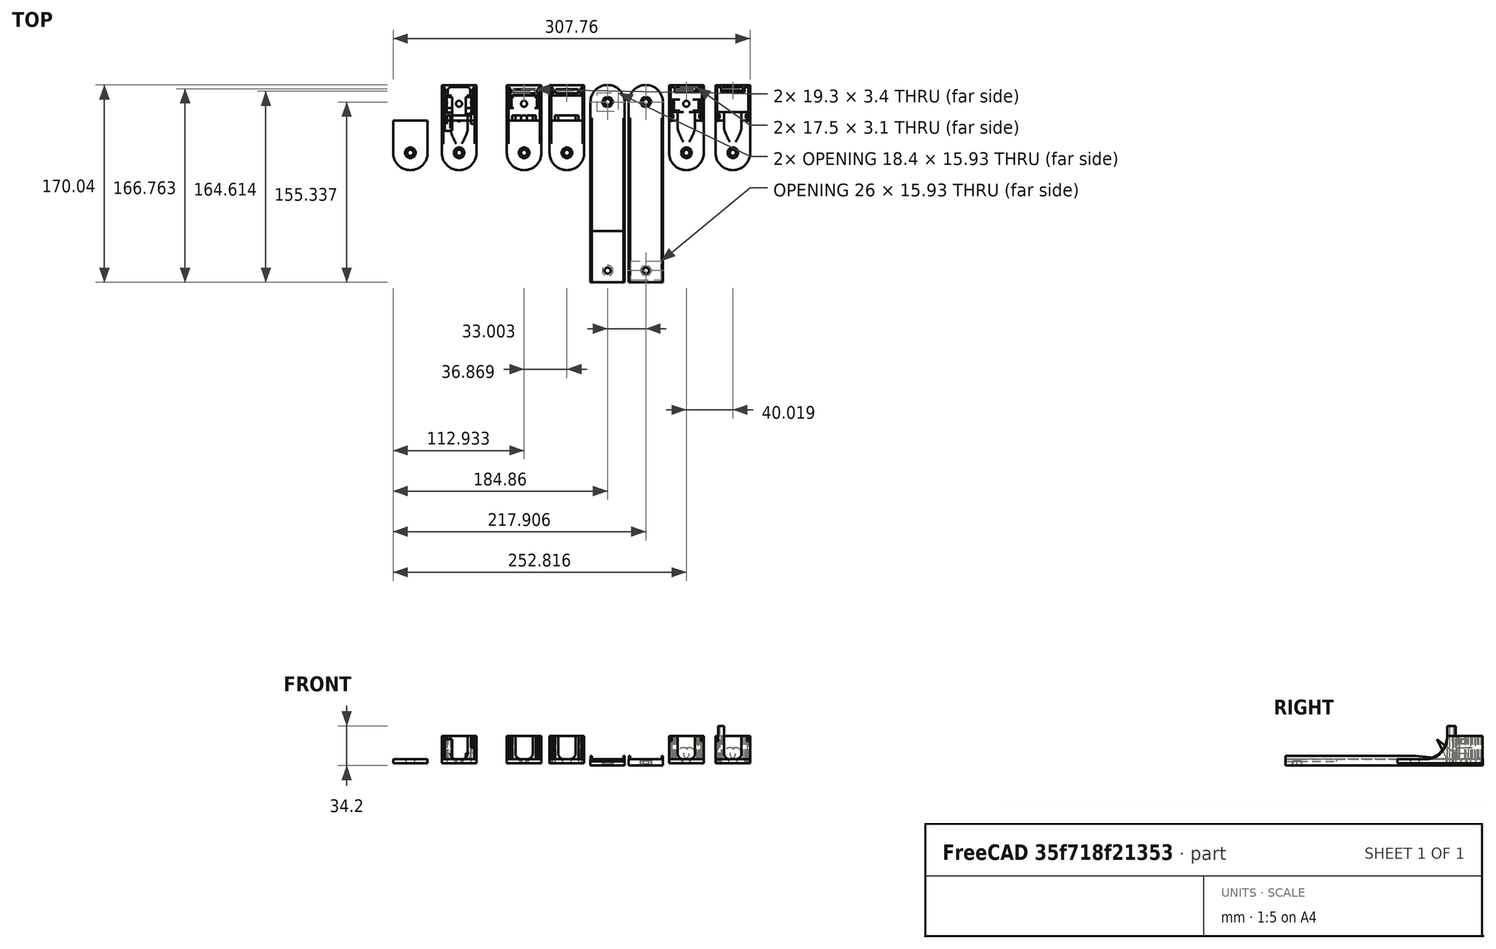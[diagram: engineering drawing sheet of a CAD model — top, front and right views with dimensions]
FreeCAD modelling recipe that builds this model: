
FCSTD DOCUMENT  (FreeCAD 0.18.4R)
Label: tmp
License: All rights reserved
LicenseURL: http://en.wikipedia.org/wiki/All_rights_reserved
objects: Part::Extrusion×56, Part::Part2DObjectPython×44, Part::Cut×42, Part::Feature×31, Part::FeaturePython×31, Part::MultiFuse×22, App::DocumentObjectGroup×10, Part::Cone×1
note: 227 computed .brp shape members not serialized (recipe doc carries the construction recipe); baked Part::Feature solids carry a one-line shape summary decoded from their .brp

FEATURE [Part::MultiFuse] Fusion
FEATURE [Part::Part2DObjectPython] Rectangle008  # Draft 2D object (typed FeaturePython)
  ChamferSize = 0
  Columns = 1
  FilletRadius = 0
  Height = 8.73003
  Length = 8.98196
  MakeFace = true
  Placement = pos=(-698.896,-12.7746,7.63603) rot=(0.57735,0.57735,0.57735;2.0944rad)
  Rows = 1
FEATURE [Part::Part2DObjectPython] Circle  # Draft 2D object (typed FeaturePython)
  FirstAngle = 0
  LastAngle = 0
  MakeFace = true
  Placement = pos=(-707.421,-8.97512,-3.63395) rot=(0,0,1;0rad)
  Radius = 2.6
  Support = -> [Fusion]
FEATURE [Part::Extrusion] Extrusion
  Base = -> Circle
  Dir = (0,0,-104.516)
  DirMode = 0
  FaceMakerClass = Part::FaceMakerBullseye
  LengthFwd = 0
  LengthRev = 0
  Solid = true
  Symmetric = false
FEATURE [Part::Feature] Face001
  Placement = pos=(-176.911,1.4e-14,3.6e-14) rot=(0,0,1;0rad)
  shape: bbox 5 x 7.4 x 3e-07 mm, 1 faces, 0 solids (baked)
FEATURE [Part::Cut] Cut004006005004002008019023005014
FEATURE [Part::Feature] Face003
  Placement = pos=(86.8688,-7e-15,-1.8e-14) rot=(0,0,1;0rad)
  shape: bbox 3.179 x 4.601 x 4.951e-06 mm, 1 faces, 0 solids (baked)
FEATURE [Part::Feature] Face
  shape: bbox 29.86 x 30.4 x 3e-07 mm, 1 faces, 0 solids (baked)
FEATURE [Part::Extrusion] Extrusion003
  Base = -> Face
  Dir = (1.2e-15,1.59e-14,-8.7)
  DirMode = 0
  FaceMakerClass = Part::FaceMakerBullseye
  LengthFwd = 0
  LengthRev = 0
  Solid = true
  Symmetric = false
FEATURE [Part::Feature] Face004
  Placement = pos=(86.8688,-7e-15,-1.8e-14) rot=(0,0,1;0rad)
  shape: bbox 3.308 x 4.601 x 4.951e-06 mm, 1 faces, 0 solids (baked)
FEATURE [Part::Part2DObjectPython] Rectangle  # Draft 2D object (typed FeaturePython)
  ChamferSize = 0
  Columns = 1
  FilletRadius = 0
  Height = 3.10055
  Length = 17.5
  MakeFace = true
  Placement = pos=(-716.1,2.42323,16.3661) rot=(0,0,1;0rad)
  Rows = 1
FEATURE [Part::Extrusion] Extrusion001
  Base = -> Rectangle
  Dir = (2.96e-14,4.57e-14,-64.3884)
  DirMode = 0
  FaceMakerClass = Part::FaceMakerBullseye
  LengthFwd = 0
  LengthRev = 0
  Solid = true
  Symmetric = false
FEATURE [Part::Feature] Face006
  Placement = pos=(-756.265,0.89093,29.4029) rot=(1,0,0;1.5708rad)
  shape: bbox 4.243e-07 x 5.5 x 4 mm, 1 faces, 0 solids (baked)
FEATURE [Part::Extrusion] Extrusion019
  Base = -> Face006
  Dir = (-0.5,3.05e-14,0)
  DirMode = 0
  FaceMakerClass = Part::FaceMakerBullseye
  LengthFwd = 0
  LengthRev = 0
  Solid = true
  Symmetric = false
FEATURE [Part::Cut] Cut
  Base = -> Fusion
  Tool = -> Extrusion
FEATURE [Part::Cut] Cut001
  Base = -> Cut
  Placement = pos=(135.846,-2.34e-13,1.41e-13) rot=(0,0,1;0rad)
  Tool = -> Extrusion001
FEATURE [Part::Extrusion] Extrusion006
  Base = -> Face003
  Dir = (1.13e-14,3.35e-14,-10.0532)
  DirMode = 0
  FaceMakerClass = Part::FaceMakerBullseye
  LengthFwd = 0
  LengthRev = 0
  Solid = true
  Symmetric = false
FEATURE [Part::Extrusion] Extrusion007
  Base = -> Face004
  Dir = (1.43e-14,4.44e-14,-13.335)
  DirMode = 0
  FaceMakerClass = Part::FaceMakerBullseye
  LengthFwd = 0
  LengthRev = 0
  Solid = true
  Symmetric = false
FEATURE [Part::Feature] Face005
  Placement = pos=(-756.265,0.89093,29.4029) rot=(1,0,0;1.5708rad)
  shape: bbox 4.243e-07 x 5 x 4 mm, 1 faces, 0 solids (baked)
FEATURE [Part::Extrusion] Extrusion018
  Base = -> Face005
  Dir = (0.5,-3.05e-14,0)
  DirMode = 0
  FaceMakerClass = Part::FaceMakerBullseye
  LengthFwd = 0
  LengthRev = 0
  Solid = true
  Symmetric = false
FEATURE [Part::Cut] Cut004006005004002008019023005004
  Placement = pos=(-176.911,1.4e-14,3.6e-14) rot=(0,0,1;0rad)
FEATURE [Part::MultiFuse] Fusion002005
  Placement = pos=(86.8688,-7.1e-15,-1.78e-14) rot=(0,0,1;0rad)
FEATURE [Part::Feature] Face002
  Placement = pos=(-176.911,1.4e-14,3.6e-14) rot=(0,0,1;0rad)
  shape: bbox 5 x 7.4 x 3e-07 mm, 1 faces, 0 solids (baked)
FEATURE [Part::Extrusion] Extrusion005
  Base = -> Face002
  Dir = (2.184e-13,5.98e-14,-8.7)
  DirMode = 0
  FaceMakerClass = Part::FaceMakerBullseye
  LengthFwd = 0
  LengthRev = 0
  Solid = true
  Symmetric = false
FEATURE [Part::Extrusion] Extrusion004
  Base = -> Face001
  Dir = (-2.51e-14,6.47e-14,-8.7)
  DirMode = 0
  FaceMakerClass = Part::FaceMakerBullseye
  LengthFwd = 0
  LengthRev = 0
  Solid = true
  Symmetric = false
FEATURE [Part::Part2DObjectPython] Rectangle007  # Draft 2D object (typed FeaturePython)
  ChamferSize = 0
  Columns = 1
  FilletRadius = 0
  Height = 2
  Length = 2
  MakeFace = true
  Placement = pos=(-698.896,-12.7746,-3.63395) rot=(1,0,0;1.5708rad)
  Rows = 1
FEATURE [Part::Extrusion] Extrusion015
  Base = -> Rectangle007
  Dir = (6.992e-13,9.7,-2.2e-15)
  DirMode = 0
  FaceMakerClass = Part::FaceMakerBullseye
  LengthFwd = 0
  LengthRev = 0
  Solid = true
  Symmetric = false
FEATURE [Part::Part2DObjectPython] Rectangle009  # Draft 2D object (typed FeaturePython)
  ChamferSize = 0
  Columns = 1
  FilletRadius = 0
  Height = 8.52247
  Length = 8.85872
  MakeFace = true
  Placement = pos=(-723.896,-3.91585,7.84359) rot=(0.57735,-0.57735,-0.57735;2.0944rad)
  Rows = 1
FEATURE [Part::Part2DObjectPython] Rectangle001  # Draft 2D object (typed FeaturePython)
  ChamferSize = 0
  Columns = 1
  FilletRadius = 0
  Height = 3.10055
  Length = 17.5
  MakeFace = true
  Placement = pos=(-676.081,2.42323,25.0661) rot=(0,0,1;0rad)
  Rows = 1
  Support = -> [Cut001]
FEATURE [Part::Extrusion] Extrusion002
  Base = -> Rectangle001
  Dir = (2.04e-14,3.15e-14,-44.3555)
  DirMode = 0
  FaceMakerClass = Part::FaceMakerBullseye
  LengthFwd = 0
  LengthRev = 0
  Solid = true
  Symmetric = false
FEATURE [Part::Cut] Cut004006005004002008019023005005
  Base = -> Cut004006005004002008019023005004
  Tool = -> Extrusion002
FEATURE [Part::Cut] Cut004006005004002008019023005006
  Base = -> Cut004006005004002008019023005005
  Tool = -> Extrusion003
FEATURE [Part::Cut] Cut004006005004002008019023005007
  Base = -> Cut004006005004002008019023005006
  Placement = pos=(135.846,-2.34e-13,1.41e-13) rot=(0,0,1;0rad)
  Tool = -> Extrusion005
FEATURE [Part::Cut] Cut004006005004002008019023005008
  Base = -> Cut004006005004002008019023005007
  Tool = -> Extrusion004
FEATURE [Part::MultiFuse] Fusion005002002014004003003002009002010004002003006003008008004007002004006006004008003005011006
  Placement = pos=(-82.9949,0,-5e-15) rot=(0,0,1;0rad)
  Shapes = -> [Cut004006005004002008019023005007]
FEATURE [Part::Part2DObjectPython] Rectangle002  # Draft 2D object (typed FeaturePython)
  ChamferSize = 0
  Columns = 1
  FilletRadius = 0
  Height = 20
  Length = 5.5
  MakeFace = true
  Placement = pos=(-705.896,-12.7746,-3.63395) rot=(1,0,0;1.5708rad)
  Rows = 1
  Support = -> [Cut004006005004002008019023005014]
FEATURE [Part::Extrusion] Extrusion008
  Base = -> Rectangle002
  Dir = (6.992e-13,9.7,-2.2e-15)
  DirMode = 0
  FaceMakerClass = Part::FaceMakerBullseye
  LengthFwd = 0
  LengthRev = 0
  Solid = true
  Symmetric = false
FEATURE [Part::Cut] Cut004006005004002008019023005017
  Base = -> Cut004006005004002008019023005014
  Tool = -> Extrusion008
FEATURE [Part::Part2DObjectPython] Rectangle003  # Draft 2D object (typed FeaturePython)
  ChamferSize = 0
  Columns = 1
  FilletRadius = 0
  Height = 20
  Length = 5.5
  MakeFace = true
  Placement = pos=(-716.896,-12.7746,16.3661) rot=(0,0.707107,-0.707107;3.14159rad)
  Rows = 1
  Support = -> [Cut004006005004002008019023005017]
FEATURE [Part::Extrusion] Extrusion009
  Base = -> Rectangle003
  Dir = (6.24e-13,9.7,-4.3e-15)
  DirMode = 0
  FaceMakerClass = Part::FaceMakerBullseye
  LengthFwd = 0
  LengthRev = 0
  Solid = true
  Symmetric = false
FEATURE [Part::Cut] Cut004006005004002008019023005018
  Base = -> Cut004006005004002008019023005017
  Tool = -> Extrusion009
FEATURE [Part::Part2DObjectPython] Rectangle005  # Draft 2D object (typed FeaturePython)
  ChamferSize = 0
  Columns = 1
  FilletRadius = 0
  Height = 2
  Length = 2
  MakeFace = true
  Placement = pos=(-720.396,-12.7746,-1.63395) rot=(0,0.707107,-0.707107;3.14159rad)
  Rows = 1
  Support = -> [Cut004006005004002008019023005018]
FEATURE [Part::Part2DObjectPython] Circle001  # Draft 2D object (typed FeaturePython)
  FirstAngle = 0
  LastAngle = 0
  MakeFace = true
  Placement = pos=(-725.896,-12.7746,-1.63395) rot=(0,0.707107,-0.707107;3.14159rad)
  Radius = 2
  Support = -> [Cut004006005004002008019023005018]
FEATURE [Part::Extrusion] Extrusion012
  Base = -> Rectangle005
  Dir = (6.24e-13,9.7,-4.3e-15)
  DirMode = 0
  FaceMakerClass = Part::FaceMakerBullseye
  LengthFwd = 0
  LengthRev = 0
  Solid = true
  Symmetric = false
FEATURE [Part::Part2DObjectPython] Circle002  # Draft 2D object (typed FeaturePython)
  FirstAngle = 0
  LastAngle = 0
  MakeFace = true
  Placement = pos=(-720.396,-12.7746,-1.63395) rot=(0,0.707107,-0.707107;3.14159rad)
  Radius = 2
  Support = -> [Extrusion012]
FEATURE [Part::Extrusion] Extrusion013
  Base = -> Circle002
  Dir = (6.367e-13,9.7,-2.2e-15)
  DirMode = 0
  FaceMakerClass = Part::FaceMakerBullseye
  LengthFwd = 0
  LengthRev = 0
  Solid = true
  Symmetric = false
FEATURE [Part::Part2DObjectPython] Rectangle004  # Draft 2D object (typed FeaturePython)
  ChamferSize = 0
  Columns = 1
  FilletRadius = 0
  Height = 2
  Length = 2
  MakeFace = true
  Placement = pos=(-723.896,-12.7746,-1.63395) rot=(0,0.707107,-0.707107;3.14159rad)
  Rows = 1
  Support = -> [Cut004006005004002008019023005018]
FEATURE [Part::Extrusion] Extrusion010
  Base = -> Rectangle004
  Dir = (6.24e-13,9.7,-4.3e-15)
  DirMode = 0
  FaceMakerClass = Part::FaceMakerBullseye
  LengthFwd = 0
  LengthRev = 0
  Solid = true
  Symmetric = false
FEATURE [Part::Extrusion] Extrusion011
  Base = -> Circle001
  Dir = (6.367e-13,9.7,-2.2e-15)
  DirMode = 0
  FaceMakerClass = Part::FaceMakerBullseye
  LengthFwd = 0
  LengthRev = 0
  Solid = true
  Symmetric = false
FEATURE [Part::Cut] Cut004006005004002008019023005019
  Base = -> Extrusion010
  Tool = -> Extrusion011
FEATURE [Part::MultiFuse] Fusion005002002014004003003002009002010004002003006003008008004007002004003
  Placement = pos=(-677.592,-2.54468,-4) rot=(0,0,1;0rad)
FEATURE [Part::Cut] Cut004006005004002008019023005020
  Base = -> Extrusion012
  Tool = -> Extrusion013
FEATURE [Part::MultiFuse] Fusion005002002014004003003002009002010004002003006003008008004007002004006006004008003005011007
  Shapes = -> [Cut004006005004002008019023005019,Cut004006005004002008019023005020,Cut004006005004002008019023005018]
FEATURE [Part::Part2DObjectPython] Rectangle006  # Draft 2D object (typed FeaturePython)
  ChamferSize = 0
  Columns = 1
  FilletRadius = 0
  Height = 2
  Length = 2
  MakeFace = true
  Placement = pos=(-702.396,-12.7746,-3.63395) rot=(1,0,0;1.5708rad)
  Rows = 1
  Support = -> [Fusion005002002014004003003002009002010004002003006003008008004007002004006006004008003005011007]
FEATURE [Part::Extrusion] Extrusion014
  Base = -> Rectangle006
  Dir = (6.992e-13,9.7,-2.2e-15)
  DirMode = 0
  FaceMakerClass = Part::FaceMakerBullseye
  LengthFwd = 0
  LengthRev = 0
  Solid = true
  Symmetric = false
FEATURE [Part::Part2DObjectPython] Circle003  # Draft 2D object (typed FeaturePython)
  FirstAngle = 0
  LastAngle = 0
  MakeFace = true
  Placement = pos=(-702.396,-12.7746,-1.63395) rot=(1,0,0;1.5708rad)
  Radius = 2
  Support = -> [Rectangle006]
FEATURE [Part::Extrusion] Extrusion017
  Base = -> Circle003
  Dir = (6.992e-13,9.7,-2.2e-15)
  DirMode = 0
  FaceMakerClass = Part::FaceMakerBullseye
  LengthFwd = 0
  LengthRev = 0
  Solid = true
  Symmetric = false
FEATURE [Part::Cut] Cut004006005004002008019023005021
  Base = -> Extrusion014
  Tool = -> Extrusion017
FEATURE [Part::Part2DObjectPython] Circle004  # Draft 2D object (typed FeaturePython)
  FirstAngle = 0
  LastAngle = 0
  MakeFace = true
  Placement = pos=(-696.896,-12.7746,-1.63395) rot=(1,0,0;1.5708rad)
  Radius = 2
  Support = -> [Fusion005002002014004003003002009002010004002003006003008008004007002004006006004008003005011007]
FEATURE [Part::Extrusion] Extrusion016
  Base = -> Circle004
  Dir = (6.992e-13,9.7,-2.2e-15)
  DirMode = 0
  FaceMakerClass = Part::FaceMakerBullseye
  LengthFwd = 0
  LengthRev = 0
  Solid = true
  Symmetric = false
FEATURE [Part::Cut] Cut004006005004002008019023005022
  Base = -> Extrusion015
  Tool = -> Extrusion016
FEATURE [Part::MultiFuse] Fusion005002002014004003003002009002010004002003006003008008004007002004006006004008003005011008
  Shapes = -> [Cut004006005004002008019023005022,Fusion005002002014004003003002009002010004002003006003008008004007002004006006004008003005011007,Cut004006005004002008019023005021]
FEATURE [Part::Cut] Cut004006005004002008019023005023
  Base = -> Fusion005002002014004003003002009002010004002003006003008008004007002004006006004008003005011008
  Tool = -> Extrusion018
FEATURE [Part::Cut] Cut004006005004002008019023005024
  Base = -> Cut004006005004002008019023005023
  Tool = -> Extrusion019
FEATURE [Part::FeaturePython] Slice  # WARN: FeaturePython — macro-defined, semantics opaque (R4)
  Base = -> Cut004006005004002008019023005024
  Mode = 1
  Tolerance = 0
  Tools = -> [Rectangle008]
FEATURE [Part::FeaturePython] Slice_child0  label="Slice.0"  # WARN: FeaturePython — macro-defined, semantics opaque (R4)
  Base = -> Slice
  FilterType = 1
  Invert = false
  OverrideMaxVal = 0
  WindowFrom = 80
  WindowTo = 100
  items = 0
FEATURE [Part::FeaturePython] Slice001  # WARN: FeaturePython — macro-defined, semantics opaque (R4)
  Base = -> Slice_child0
  Mode = 1
  Tolerance = 0
  Tools = -> [Rectangle009]
FEATURE [Part::FeaturePython] Slice001_child1  label="Slice001.1"  # WARN: FeaturePython — macro-defined, semantics opaque (R4)
  Base = -> Slice001
  FilterType = 1
  Invert = false
  OverrideMaxVal = 0
  Placement = pos=(0,0,-1) rot=(0,0,1;0rad)
  WindowFrom = 80
  WindowTo = 100
  items = 1
FEATURE [Part::FeaturePython] Slice_child1  label="Slice.1"  # WARN: FeaturePython — macro-defined, semantics opaque (R4)
  Base = -> Slice
  FilterType = 1
  Invert = false
  OverrideMaxVal = 0
  Placement = pos=(0,0,-1) rot=(0,0,1;0rad)
  WindowFrom = 80
  WindowTo = 100
  items = 1
FEATURE [Part::FeaturePython] Slice001_child0  label="Slice001.0"  # WARN: FeaturePython — macro-defined, semantics opaque (R4)
  Base = -> Slice001
  FilterType = 1
  Invert = false
  OverrideMaxVal = 0
  WindowFrom = 80
  WindowTo = 100
  items = 0
FEATURE [Part::MultiFuse] Fusion005002002014004003003002009002010004002003006003008008004007002004006006004008003005011009
  Shapes = -> [Slice001_child0,Slice001_child1]
FEATURE [Part::MultiFuse] Fusion005002002014004003003002009002010004002003006003008008004007002004006006004008003005011010
  Shapes = -> [Slice_child1,Fusion005002002014004003003002009002010004002003006003008008004007002004006006004008003005011009]
FEATURE [App::DocumentObjectGroup] GrExplode_Slice001  label="Exploded Slice001"
  Group = -> [Fusion005002002014004003003002009002010004002003006003008008004007002004006006004008003005011010]
FEATURE [App::DocumentObjectGroup] GrExplode_Slice  label="Exploded Slice"
  Group = -> [Slice_child0]
FEATURE [Part::Cut] Cut004006005004002008019023005015
  Base = -> Fusion002005
  Tool = -> Extrusion006
FEATURE [Part::Cut] Cut004006005004002008019023005016
  Base = -> Cut004006005004002008019023005015
  Tool = -> Extrusion007
FEATURE [Part::Feature] Slice_child0001  label="Slice.001"
  shape: bbox 29.86 x 30.4 x 23.5 mm, 73 faces (baked)
FEATURE [Part::Part2DObjectPython] Rectangle010  # Draft 2D object (typed FeaturePython)
  ChamferSize = 0
  Columns = 1
  FilletRadius = 0
  Height = 195
  Length = 50
  MakeFace = true
  Placement = pos=(-745.304,-23.4762,-145.384) rot=(1,0,0;1.5708rad)
  Rows = 1
  Support = -> [Fusion005002002014004003003002009002010004002003006003008008004007002004006006004008003005011010]
FEATURE [Part::FeaturePython] Slice002  # WARN: FeaturePython — macro-defined, semantics opaque (R4)
  Base = -> Fusion005002002014004003003002009002010004002003006003008008004007002004006006004008003005011010
  Mode = 1
  Tolerance = 0
  Tools = -> [Rectangle010]
FEATURE [Part::FeaturePython] Slice002_child0  label="Slice002.0"  # WARN: FeaturePython — macro-defined, semantics opaque (R4)
  Base = -> Slice002
  FilterType = 1
  Invert = false
  OverrideMaxVal = 0
  WindowFrom = 80
  WindowTo = 100
  items = 0
FEATURE [Part::Part2DObjectPython] Rectangle011  # Draft 2D object (typed FeaturePython)
  ChamferSize = 0
  Columns = 1
  FilletRadius = 0
  Height = 227
  Length = 38
  MakeFace = true
  Placement = pos=(-694.304,-23.4762,-131.384) rot=(1,0,0;1.5708rad)
  Rows = 1
FEATURE [Part::FeaturePython] Slice003  # WARN: FeaturePython — macro-defined, semantics opaque (R4)
  Base = -> Cut004006005004002008019023005016
  Mode = 1
  Tolerance = 0
  Tools = -> [Rectangle011]
FEATURE [Part::FeaturePython] Slice003_child1  label="Slice003.1"  # WARN: FeaturePython — macro-defined, semantics opaque (R4)
  Base = -> Slice003
  FilterType = 1
  Invert = false
  OverrideMaxVal = 0
  WindowFrom = 80
  WindowTo = 100
  items = 1
FEATURE [Part::FeaturePython] Slice003_child2  label="Slice003.2"  # WARN: FeaturePython — macro-defined, semantics opaque (R4)
  Base = -> Slice003
  FilterType = 1
  Invert = false
  OverrideMaxVal = 0
  WindowFrom = 80
  WindowTo = 100
  items = 2
FEATURE [Part::Part2DObjectPython] Rectangle012  # Draft 2D object (typed FeaturePython)
  ChamferSize = 0
  Columns = 1
  FilletRadius = 0
  Height = 27.7492
  Length = 29.8587
  MakeFace = true
  Placement = pos=(-726.259,-23.4762,-7.13395) rot=(1,0,0;3.14159rad)
  Rows = 1
FEATURE [Part::Extrusion] Extrusion020
  Base = -> Rectangle012
  Dir = (3e-16,-8e-16,3.5)
  DirMode = 0
  FaceMakerClass = Part::FaceMakerBullseye
  LengthFwd = 0
  LengthRev = 0
  Solid = true
  Symmetric = false
FEATURE [Part::Part2DObjectPython] Circle005  # Draft 2D object (typed FeaturePython)
  FirstAngle = 0
  LastAngle = 0
  MakeFace = true
  Placement = pos=(-711.33,-51.2254,-3.63395) rot=(0,0,-1;1.5708rad)
  Radius = 14.9294
  Support = -> [Extrusion020]
FEATURE [Part::Extrusion] Extrusion021
  Base = -> Circle005
  Dir = (-3e-16,8e-16,-3.5)
  DirMode = 0
  FaceMakerClass = Part::FaceMakerBullseye
  LengthFwd = 0
  LengthRev = 0
  Solid = true
  Symmetric = false
FEATURE [Part::MultiFuse] Fusion005002002014004003003002009002010004002003006003008008004007002004006006004008003005011011
  Shapes = -> [Extrusion020,Extrusion021]
FEATURE [Part::Cone] Cone
  Angle = 360
  AttacherType = Attacher::AttachEngine3D
  Height = 3.5
  Placement = pos=(-711.33,-51.2254,-7.13395) rot=(0,0,1;0rad)
  Radius1 = 2.6
  Radius2 = 4.55
FEATURE [Part::Cut] Cut004006005004002008019023005025
  Base = -> Fusion005002002014004003003002009002010004002003006003008008004007002004006006004008003005011011
  Tool = -> Cone
FEATURE [Part::Feature] Cut004006005004002008019023005025003  label="Cut004006005004002008019023005028"
  Placement = pos=(-98.0646,4e-15,4e-15) rot=(0,0,1;0rad)
  shape: bbox 29.86 x 42.68 x 3.5 mm, 7 faces (baked)
FEATURE [Part::Feature] Cut004006005004002008019023005025004  label="Cut004006005004002008019023005029"
  Placement = pos=(-56.0646,4e-15,0) rot=(0,0,1;0rad)
  shape: bbox 29.86 x 42.68 x 3.5 mm, 7 faces (baked)
FEATURE [Part::Part2DObjectPython] Rectangle013  # Draft 2D object (typed FeaturePython)
  ChamferSize = 0
  Columns = 1
  FilletRadius = 0
  Height = 20
  Length = 20
  MakeFace = true
  Placement = pos=(-782.324,-23.4762,-3.63395) rot=(0.57735,-0.57735,-0.57735;2.0944rad)
  Rows = 1
FEATURE [Part::Part2DObjectPython] Circle006  # Draft 2D object (typed FeaturePython)
  FirstAngle = 0
  LastAngle = 0
  MakeFace = true
  Placement = pos=(-782.324,-43.4762,16.3661) rot=(0.57735,-0.57735,-0.57735;2.0944rad)
  Radius = 20
  Support = -> [Rectangle013]
FEATURE [Part::Extrusion] Extrusion022
  Base = -> Rectangle013
  Dir = (1.3716,0,0)
  DirMode = 0
  FaceMakerClass = Part::FaceMakerBullseye
  LengthFwd = 0
  LengthRev = 0
  Solid = true
  Symmetric = false
FEATURE [Part::Extrusion] Extrusion023
  Base = -> Circle006
  Dir = (1.3716,0,0)
  DirMode = 0
  FaceMakerClass = Part::FaceMakerBullseye
  LengthFwd = 0
  LengthRev = 0
  Solid = true
  Symmetric = false
FEATURE [Part::Cut] Cut004006005004002008019023005025005
  Base = -> Extrusion022
  Tool = -> Extrusion023
FEATURE [Part::Cut] Cut004006005004002008019023005025006
  Base = -> Extrusion022
  Tool = -> Extrusion023
FEATURE [Part::Part2DObjectPython] Rectangle014  # Draft 2D object (typed FeaturePython)
  ChamferSize = 0
  Columns = 1
  FilletRadius = 0
  Height = 20
  Length = 20
  MakeFace = true
  Placement = pos=(-752.465,-43.4762,-3.63395) rot=(0.57735,0.57735,0.57735;2.0944rad)
  Rows = 1
  Support = -> [Slice_child0001]
FEATURE [Part::Extrusion] Extrusion024
  Base = -> Rectangle014
  Dir = (-1.5,0,0)
  DirMode = 0
  FaceMakerClass = Part::FaceMakerBullseye
  LengthFwd = 0
  LengthRev = 0
  Solid = true
  Symmetric = false
FEATURE [Part::Part2DObjectPython] Circle007  # Draft 2D object (typed FeaturePython)
  FirstAngle = 0
  LastAngle = 0
  MakeFace = true
  Placement = pos=(-752.465,-43.4762,16.3661) rot=(0.57735,0.57735,0.57735;2.0944rad)
  Radius = 20
  Support = -> [Extrusion024]
FEATURE [Part::Extrusion] Extrusion025
  Base = -> Circle007
  Dir = (-1.5,0,0)
  DirMode = 0
  FaceMakerClass = Part::FaceMakerBullseye
  LengthFwd = 0
  LengthRev = 0
  Solid = true
  Symmetric = false
FEATURE [Part::Cut] Cut004006005004002008019023005025007
  Base = -> Extrusion024
  Tool = -> Extrusion025
FEATURE [Part::MultiFuse] Fusion005002002014004003003002009002010004002003006003008008004007002004006006004008003005011012
  Shapes = -> [Cut004006005004002008019023005025005,Cut004006005004002008019023005025007,Cut004006005004002008019023005025004]
FEATURE [Part::Feature] Fusion005002002014004003003002009002010004002003006003008008004007002004006006004008003005011012001  label="Fusion005002002014004003003002009002010004002003006003008008004007002004006006004008003005011013"
  Placement = pos=(56.0646,0,0) rot=(0,0,1;0rad)
  shape: bbox 29.86 x 42.68 x 23.5 mm, 11 faces (baked)
FEATURE [Part::Feature] Fusion005002002014004003003002009002010004002003006003008008004007002004006006004008003005011012002  label="Fusion005002002014004003003002009002010004002003006003008008004007002004006006004008003005011014"
  Placement = pos=(92.9335,0,-1.78e-14) rot=(0,0,1;0rad)
  shape: bbox 29.86 x 42.68 x 23.5 mm, 11 faces (baked)
FEATURE [Part::Feature] Fusion005002002014004003003002009002010004002003006003008008004007002004006006004008003005011012003  label="Fusion005002002014004003003002009002010004002003006003008008004007002004006006004008003005011015"
  shape: bbox 29.86 x 42.68 x 23.5 mm, 11 faces (baked)
FEATURE [Part::MultiFuse] Fusion005002002014004003003002009002010004002003006003008008004007002004006006004008003005011012004
  Shapes = -> [Fusion005002002014004003003002009002010004002003006003008008004007002004006006004008003005011012002,Slice003_child1]
FEATURE [App::DocumentObjectGroup] GrExplode_Slice003  label="Exploded Slice003"
  Group = -> [Slice003_child2,Fusion005002002014004003003002009002010004002003006003008008004007002004006006004008003005011012004]
FEATURE [Part::MultiFuse] Fusion005002002014004003003002009002010004002003006003008008004007002004006006004008003005011012005
  Shapes = -> [Fusion005002002014004003003002009002010004002003006003008008004007002004006006004008003005011012001,Slice002_child0]
FEATURE [App::DocumentObjectGroup] GrExplode_Slice002  label="Exploded Slice002"
  Group = -> [Fusion005002002014004003003002009002010004002003006003008008004007002004006006004008003005011012005]
FEATURE [Part::MultiFuse] Fusion005002002014004003003002009002010004002003006003008008004007002004006006004008003005011012006
  Shapes = -> [Fusion005002002014004003003002009002010004002003006003008008004007002004006006004008003005011012003,Slice_child0001]
FEATURE [Part::Part2DObjectPython] Rectangle015  # Draft 2D object (typed FeaturePython)
  ChamferSize = 0
  Columns = 1
  FilletRadius = 0
  Height = 10
  Length = 9.7
  MakeFace = true
  Placement = pos=(-584.074,-5.17567,6.36605) rot=(0.57735,-0.57735,-0.57735;2.0944rad)
  Rows = 1
  Support = -> [Cut001]
FEATURE [Part::FeaturePython] Slice004  # WARN: FeaturePython — macro-defined, semantics opaque (R4)
  Base = -> Cut001
  Mode = 1
  Tolerance = 0
  Tools = -> [Rectangle015]
FEATURE [Part::FeaturePython] Slice004_child0  label="Slice004.0"  # WARN: FeaturePython — macro-defined, semantics opaque (R4)
  Base = -> Slice004
  FilterType = 1
  Invert = false
  OverrideMaxVal = 0
  WindowFrom = 80
  WindowTo = 100
  items = 0
FEATURE [App::DocumentObjectGroup] GrExplode_Slice004  label="Exploded Slice004"
  Group = -> [Slice004_child0]
FEATURE [Part::FeaturePython] Slice004_child1  label="Slice004.1"  # WARN: FeaturePython — macro-defined, semantics opaque (R4)
  Base = -> Slice004
  FilterType = 1
  Invert = false
  OverrideMaxVal = 0
  Placement = pos=(0,-1.8e-15,-1) rot=(0,0,1;0rad)
  WindowFrom = 80
  WindowTo = 100
  items = 1
FEATURE [Part::Part2DObjectPython] Rectangle016  # Draft 2D object (typed FeaturePython)
  ChamferSize = 0
  Columns = 1
  FilletRadius = 0
  Height = 10
  Length = 9.7
  MakeFace = true
  Placement = pos=(-559.074,-14.8757,6.36605) rot=(0.57735,0.57735,0.57735;2.0944rad)
  Rows = 1
  Support = -> [Slice004_child0]
FEATURE [Part::FeaturePython] Slice005  # WARN: FeaturePython — macro-defined, semantics opaque (R4)
  Base = -> Slice004_child0
  Mode = 1
  Tolerance = 0
  Tools = -> [Rectangle016]
FEATURE [Part::FeaturePython] Slice005_child0  label="Slice005.0"  # WARN: FeaturePython — macro-defined, semantics opaque (R4)
  Base = -> Slice005
  FilterType = 1
  Invert = false
  OverrideMaxVal = 0
  WindowFrom = 80
  WindowTo = 100
  items = 0
FEATURE [Part::FeaturePython] Slice005_child1  label="Slice005.1"  # WARN: FeaturePython — macro-defined, semantics opaque (R4)
  Base = -> Slice005
  FilterType = 1
  Invert = false
  OverrideMaxVal = 0
  Placement = pos=(0,-0.500548,-1) rot=(0,0,1;0rad)
  WindowFrom = 80
  WindowTo = 100
  items = 1
FEATURE [Part::MultiFuse] Fusion005002002014004003003002009002010004002003006003008008004007002004006006004008003005011012007
  Shapes = -> [Slice004_child1,Slice005_child0]
FEATURE [Part::MultiFuse] Fusion005002002014004003003002009002010004002003006003008008004007002004006006004008003005011012008
  Shapes = -> [Fusion005002002014004003003002009002010004002003006003008008004007002004006006004008003005011012007,Slice005_child1]
FEATURE [Part::Part2DObjectPython] Rectangle017  # Draft 2D object (typed FeaturePython)
  ChamferSize = 0
  Columns = 1
  FilletRadius = 0
  Height = 165
  Length = 85
  MakeFace = true
  Placement = pos=(-823.452,-23.4762,-66.1339) rot=(1,0,0;1.5708rad)
  Rows = 1
  Support = -> [Fusion005002002014004003003002009002010004002003006003008008004007002004006006004008003005011012006]
FEATURE [Part::FeaturePython] Slice006  # WARN: FeaturePython — macro-defined, semantics opaque (R4)
  Base = -> Fusion005002002014004003003002009002010004002003006003008008004007002004006006004008003005011012006
  Mode = 1
  Tolerance = 0
  Tools = -> [Rectangle017]
FEATURE [Part::FeaturePython] Slice006_child0  label="Slice006.0"  # WARN: FeaturePython — macro-defined, semantics opaque (R4)
  Base = -> Slice006
  FilterType = 1
  Invert = false
  OverrideMaxVal = 0
  WindowFrom = 80
  WindowTo = 100
  items = 0
FEATURE [Part::FeaturePython] Slice006_child1  label="Slice006.1"  # WARN: FeaturePython — macro-defined, semantics opaque (R4)
  Base = -> Slice006
  FilterType = 1
  Invert = false
  OverrideMaxVal = 0
  WindowFrom = 80
  WindowTo = 100
  items = 1
FEATURE [Part::Part2DObjectPython] Rectangle018  # Draft 2D object (typed FeaturePython)
  ChamferSize = 0
  Columns = 1
  FilletRadius = 0
  Height = 11.7562
  Length = 25.4553
  MakeFace = true
  Placement = pos=(-780.407,-13.6324,-3.63395) rot=(0,0,1;0rad)
  Rows = 1
FEATURE [Part::FeaturePython] Slice007  # WARN: FeaturePython — macro-defined, semantics opaque (R4)
  Base = -> Slice006_child0
  Mode = 1
  Tolerance = 0
  Tools = -> [Rectangle018]
FEATURE [Part::FeaturePython] Slice007_child0  label="Slice007.0"  # WARN: FeaturePython — macro-defined, semantics opaque (R4)
  Base = -> Slice007
  FilterType = 1
  Invert = false
  OverrideMaxVal = 0
  WindowFrom = 80
  WindowTo = 100
  items = 0
FEATURE [Part::FeaturePython] Slice007_child1  label="Slice007.1"  # WARN: FeaturePython — macro-defined, semantics opaque (R4)
  Base = -> Slice007
  FilterType = 1
  Invert = false
  OverrideMaxVal = 0
  Placement = pos=(-0.50409,-2.13e-14,0) rot=(0,0,1;0rad)
  WindowFrom = 80
  WindowTo = 100
  items = 1
FEATURE [Part::FeaturePython] Slice007_child2  label="Slice007.2"  # WARN: FeaturePython — macro-defined, semantics opaque (R4)
  Base = -> Slice007
  FilterType = 1
  Invert = false
  OverrideMaxVal = 0
  Placement = pos=(1.74591,-1.8e-15,3.6e-15) rot=(0,0,1;0rad)
  WindowFrom = 80
  WindowTo = 100
  items = 2
FEATURE [Part::FeaturePython] Slice007_child3  label="Slice007.3"  # WARN: FeaturePython — macro-defined, semantics opaque (R4)
  Base = -> Slice007
  FilterType = 1
  Invert = false
  OverrideMaxVal = 0
  Placement = pos=(0.508778,-1.155e-13,-1.8e-15) rot=(0,0,1;0rad)
  WindowFrom = 80
  WindowTo = 100
  items = 3
FEATURE [Part::Part2DObjectPython] Rectangle019  # Draft 2D object (typed FeaturePython)
  ChamferSize = 0
  Columns = 1
  FilletRadius = 0
  Height = 11.7562
  Length = 25.4553
  MakeFace = true
  Placement = pos=(-780.407,-13.6324,-3.63395) rot=(0,0,1;0rad)
  Rows = 1
  Support = -> [Slice007_child0]
FEATURE [Part::FeaturePython] Slice008  # WARN: FeaturePython — macro-defined, semantics opaque (R4)
  Base = -> Slice007_child0
  Mode = 1
  Tolerance = 0
  Tools = -> [Rectangle019]
FEATURE [Part::FeaturePython] Slice008_child0  label="Slice008.0"  # WARN: FeaturePython — macro-defined, semantics opaque (R4)
  Base = -> Slice008
  FilterType = 1
  Invert = false
  OverrideMaxVal = 0
  WindowFrom = 80
  WindowTo = 100
  items = 0
FEATURE [Part::FeaturePython] Slice008_child1  label="Slice008.1"  # WARN: FeaturePython — macro-defined, semantics opaque (R4)
  Base = -> Slice008
  FilterType = 1
  Invert = false
  OverrideMaxVal = 0
  Placement = pos=(-1.76886,5.51e-14,-5.3e-15) rot=(0,0,1;0rad)
  WindowFrom = 80
  WindowTo = 100
  items = 1
FEATURE [Part::Feature] Face007
  Placement = pos=(0.508778,-1.155e-13,-1.8e-15) rot=(0,0,1;0rad)
  shape: bbox 5.702e-06 x 9.7 x 20 mm, 1 faces, 0 solids (baked)
FEATURE [Part::Extrusion] Extrusion026
  Base = -> Face007
  Dir = (-0.508777,0,-1e-15)
  DirMode = 0
  FaceMakerClass = Part::FaceMakerBullseye
  LengthFwd = 0
  LengthRev = 0
  Solid = true
  Symmetric = false
FEATURE [Part::Cut] Cut004006005004002008019023005025008
  Base = -> Slice007_child3
  Placement = pos=(-0.277639,0.085352,1.69e-14) rot=(0,0,1;0rad)
  Tool = -> Extrusion026
FEATURE [Part::Feature] Face008
  Placement = pos=(-0.50409,-2.13e-14,0) rot=(0,0,1;0rad)
  shape: bbox 5.803e-06 x 9.7 x 20 mm, 1 faces, 0 solids (baked)
FEATURE [Part::Extrusion] Extrusion027
  Base = -> Face008
  Dir = (0.504089,0,1e-15)
  DirMode = 0
  FaceMakerClass = Part::FaceMakerBullseye
  LengthFwd = 0
  LengthRev = 0
  Solid = true
  Symmetric = false
FEATURE [Part::Cut] Cut004006005004002008019023005025009
  Base = -> Slice007_child1
  Placement = pos=(0.25,1.95e-14,0) rot=(0,0,1;0rad)
  Tool = -> Extrusion027
FEATURE [Part::Feature] Face009
  Placement = pos=(-0.277638,0.085352,1.41e-14) rot=(0,0,1;0rad)
  shape: bbox 5.702e-06 x 9.7 x 20 mm, 1 faces, 0 solids (baked)
FEATURE [Part::Extrusion] Extrusion028
  Base = -> Face009
  Dir = (-0.491222,0,-9e-16)
  DirMode = 0
  FaceMakerClass = Part::FaceMakerBullseye
  LengthFwd = 0
  LengthRev = 0
  Solid = true
  Symmetric = false
FEATURE [Part::Feature] Face010
  Placement = pos=(0.249999,-1.8e-15,1e-15) rot=(0,0,1;0rad)
  shape: bbox 5.803e-06 x 9.7 x 20 mm, 1 faces, 0 solids (baked)
FEATURE [Part::Extrusion] Extrusion029
  Base = -> Face010
  Dir = (0.49591,0,9e-16)
  DirMode = 0
  FaceMakerClass = Part::FaceMakerBullseye
  LengthFwd = 0
  LengthRev = 0
  Solid = true
  Symmetric = false
FEATURE [Part::Cut] Cut004006005004002008019023005025010
  Base = -> Cut004006005004002008019023005025009
  Tool = -> Extrusion029
FEATURE [Part::Cut] Cut004006005004002008019023005025011
  Base = -> Cut004006005004002008019023005025008
  Placement = pos=(0.0276394,-0.085352,-1.69e-14) rot=(0,0,1;0rad)
  Tool = -> Extrusion028
FEATURE [Part::Feature] Face011
  Placement = pos=(-55.8059,5.91e-14,-1) rot=(0,0,1;0rad)
  shape: bbox 1.5 x 5 x 1.943e-06 mm, 1 faces, 0 solids (baked)
FEATURE [Part::Extrusion] Extrusion030
  Base = -> Face011
  Dir = (0,0,-0.2)
  DirMode = 0
  FaceMakerClass = Part::FaceMakerBullseye
  LengthFwd = 0
  LengthRev = 0
  Solid = true
  Symmetric = false
FEATURE [Part::Cut] Cut004006005004002008019023005025012
  Base = -> Cut004006005004002008019023005025011
  Tool = -> Extrusion030
FEATURE [Part::Feature] Face012
  Placement = pos=(-56.3187,2.2e-15,-1) rot=(0,0,1;0rad)
  shape: bbox 1.5 x 5.5 x 1.943e-06 mm, 1 faces, 0 solids (baked)
FEATURE [Part::Extrusion] Extrusion031
  Base = -> Face012
  Dir = (0,0,-0.2)
  DirMode = 0
  FaceMakerClass = Part::FaceMakerBullseye
  LengthFwd = 0
  LengthRev = 0
  Solid = true
  Symmetric = false
FEATURE [Part::Cut] Cut004006005004002008019023005025013
  Base = -> Cut004006005004002008019023005025010
  Tool = -> Extrusion031
FEATURE [Part::Feature] Face014
  Placement = pos=(-0.741221,5.5e-14,-3.7e-15) rot=(0,0,1;0rad)
  shape: bbox 5.702e-06 x 9.7 x 20 mm, 1 faces, 0 solids (baked)
FEATURE [Part::Extrusion] Extrusion032
  Base = -> Face014
  Dir = (-1.02764,0,-1.9e-15)
  DirMode = 0
  FaceMakerClass = Part::FaceMakerBullseye
  LengthFwd = 0
  LengthRev = 0
  Solid = true
  Symmetric = false
FEATURE [Part::Cut] Cut004006005004002008019023005025014
  Base = -> Cut004006005004002008019023005025012
  Tool = -> Extrusion032
FEATURE [Part::Feature] Face015
  Placement = pos=(0.745909,-1.7e-15,1.9e-15) rot=(0,0,1;0rad)
  shape: bbox 5.803e-06 x 9.7 x 20 mm, 1 faces, 0 solids (baked)
FEATURE [Part::Extrusion] Extrusion033
  Base = -> Face015
  Dir = (1,0,1.9e-15)
  DirMode = 0
  FaceMakerClass = Part::FaceMakerBullseye
  LengthFwd = 0
  LengthRev = 0
  Solid = true
  Symmetric = false
FEATURE [Part::Cut] Cut004006005004002008019023005025015
  Base = -> Cut004006005004002008019023005025013
  Tool = -> Extrusion033
FEATURE [Part::Feature] Face016
  shape: bbox 4.243e-07 x 5 x 3.8 mm, 1 faces, 0 solids (baked)
FEATURE [Part::Extrusion] Extrusion034
  Base = -> Face016
  Dir = (0.25,-1.53e-14,0)
  DirMode = 0
  FaceMakerClass = Part::FaceMakerBullseye
  LengthFwd = 0
  LengthRev = 0
  Solid = true
  Symmetric = false
FEATURE [Part::Cut] Cut004006005004002008019023005025016
  Base = -> Cut004006005004002008019023005025014
  Tool = -> Extrusion034
FEATURE [Part::Feature] Face017
  shape: bbox 4.243e-07 x 5.5 x 3.8 mm, 1 faces, 0 solids (baked)
FEATURE [Part::Extrusion] Extrusion035
  Base = -> Face017
  Dir = (-0.258778,1.58e-14,0)
  DirMode = 0
  FaceMakerClass = Part::FaceMakerBullseye
  LengthFwd = 0
  LengthRev = 0
  Solid = true
  Symmetric = false
FEATURE [Part::Cut] Cut004006005004002008019023005025017
  Base = -> Cut004006005004002008019023005025015
  Tool = -> Extrusion035
FEATURE [App::DocumentObjectGroup] GrExplode_Slice007  label="Exploded Slice007"
  Group = -> [Slice007_child0,Slice007_child2,Cut004006005004002008019023005025016,Cut004006005004002008019023005025017]
FEATURE [Part::Part2DObjectPython] Rectangle020  # Draft 2D object (typed FeaturePython)
  ChamferSize = 0
  Columns = 1
  FilletRadius = 0
  Height = 5
  Length = 5
  MakeFace = true
  Placement = pos=(-755.215,-17.7746,-3.63395) rot=(0.57735,0.57735,0.57735;2.0944rad)
  Rows = 1
  Support = -> [Cut004006005004002008019023005025017]
FEATURE [Part::Extrusion] Extrusion036
  Base = -> Rectangle020
  Dir = (-6.5,0,0)
  DirMode = 0
  FaceMakerClass = Part::FaceMakerBullseye
  LengthFwd = 0
  LengthRev = 0
  Solid = true
  Symmetric = false
FEATURE [Part::Part2DObjectPython] Circle008  # Draft 2D object (typed FeaturePython)
  FirstAngle = 0
  LastAngle = 0
  MakeFace = true
  Placement = pos=(-761.715,-17.7746,1.36605) rot=(0.57735,-0.57735,-0.57735;2.0944rad)
  Radius = 5
  Support = -> [Extrusion036]
FEATURE [Part::Extrusion] Extrusion037
  Base = -> Circle008
  Dir = (6.5,0,0)
  DirMode = 0
  FaceMakerClass = Part::FaceMakerBullseye
  LengthFwd = 0
  LengthRev = 0
  Solid = true
  Symmetric = false
FEATURE [Part::Cut] Cut004006005004002008019023005025018
  Base = -> Extrusion036
  Tool = -> Extrusion037
FEATURE [Part::Part2DObjectPython] Wire  # Draft 2D object (typed FeaturePython)
  ChamferSize = 0
  Closed = true
  End = (-755.215,-17.7746,-3.63395)
  FilletRadius = 0
  Length = 45.6155
  MakeFace = true
  Placement = pos=(-755.215,-12.7746,-3.63395) rot=(1,0,0;1.5708rad)
  Points = (3) [(0,0,0),(-4.78874e-07,20,-3.90799e-14),(1.19719e-07,1.02141e-14,5)]
  Start = (-755.215,-12.7746,-3.63395)
  Subdivisions = 0
FEATURE [Part::Extrusion] Extrusion038
  Base = -> Wire
  Dir = (-1.5,-1.34e-14,1.3e-15)
  DirMode = 0
  FaceMakerClass = Part::FaceMakerBullseye
  LengthFwd = 0
  LengthRev = 0
  Solid = true
  Symmetric = false
FEATURE [Part::Feature] Face018
  Placement = pos=(1.74591,-1.8e-15,3.6e-15) rot=(0,0,1;0rad)
  shape: bbox 5 x 4.951e-06 x 5 mm, 1 faces, 0 solids (baked)
FEATURE [Part::Extrusion] Extrusion039
  Base = -> Face018
  Dir = (0,-5,5e-15)
  DirMode = 0
  FaceMakerClass = Part::FaceMakerBullseye
  LengthFwd = 0
  LengthRev = 0
  Solid = true
  Symmetric = false
FEATURE [Part::MultiFuse] Fusion005002002014004003003002009002010004002003006003008008004007002004006006004008003005011012009
  Shapes = -> [Extrusion038,Extrusion039]
FEATURE [Part::Part2DObjectPython] Wire001  # Draft 2D object (typed FeaturePython)
  ChamferSize = 0
  Closed = true
  End = (-755.215,-29.9723,16.5685)
  FilletRadius = 0
  Length = 49.0498
  MakeFace = true
  Placement = pos=(-755.215,-16.5246,1.36605) rot=(0.57735,0.57735,0.57735;2.0944rad)
  Points = (3) [(0,0,0),(-1.25,-5,0),(-13.4477,15.2024,0)]
  Start = (-755.215,-16.5246,1.36605)
  Subdivisions = 0
FEATURE [Part::Extrusion] Extrusion040
  Base = -> Wire001
  Dir = (-6.5,0,0)
  DirMode = 0
  FaceMakerClass = Part::FaceMakerBullseye
  LengthFwd = 0
  LengthRev = 0
  Solid = true
  Symmetric = false
FEATURE [Part::Cut] Cut004006005004002008019023005025019
  Base = -> Fusion005002002014004003003002009002010004002003006003008008004007002004006006004008003005011012009
  Tool = -> Extrusion040
FEATURE [Part::Feature] Face019
  Placement = pos=(-1.76886,5.51e-14,-5.3e-15) rot=(0,0,1;0rad)
  shape: bbox 5 x 4.951e-06 x 5 mm, 1 faces, 0 solids (baked)
FEATURE [Part::Extrusion] Extrusion041
  Base = -> Face019
  Dir = (0,-5,5e-15)
  DirMode = 0
  FaceMakerClass = Part::FaceMakerBullseye
  LengthFwd = 0
  LengthRev = 0
  Solid = true
  Symmetric = false
FEATURE [Part::Part2DObjectPython] Wire002  # Draft 2D object (typed FeaturePython)
  ChamferSize = 0
  Closed = true
  End = (-779.702,-12.7746,-3.63395)
  FilletRadius = 0
  Length = 45.6155
  MakeFace = true
  Placement = pos=(-779.702,-17.7746,-3.63395) rot=(0.57735,-0.57735,-0.57735;2.0944rad)
  Points = (3) [(0,0,0),(-5,20,-1.13687e-13),(-5,-1.11022e-14,0)]
  Start = (-779.702,-17.7746,-3.63395)
  Subdivisions = 0
  Support = -> [Cut004006005004002008019023005025016]
FEATURE [Part::Extrusion] Extrusion042
  Base = -> Wire002
  Dir = (1.47236,0,-8.4e-15)
  DirMode = 0
  FaceMakerClass = Part::FaceMakerBullseye
  LengthFwd = 0
  LengthRev = 0
  Solid = true
  Symmetric = false
FEATURE [Part::MultiFuse] Fusion005002002014004003003002009002010004002003006003008008004007002004006006004008003005011012010
  Shapes = -> [Extrusion042,Extrusion041]
FEATURE [Part::Part2DObjectPython] Wire003  # Draft 2D object (typed FeaturePython)
  ChamferSize = 0
  Closed = true
  End = (-779.702,-17.7746,-3.63395)
  FilletRadius = 0
  Length = 19.4185
  MakeFace = true
  Placement = pos=(-779.702,-16.5246,1.36605) rot=(0.57735,-0.57735,-0.57735;2.0944rad)
  Points = (3) [(0,0,0),(6.95164,-5,3.41061e-13),(1.25,-5,0)]
  Start = (-779.702,-16.5246,1.36605)
  Subdivisions = 0
  Support = -> [Fusion005002002014004003003002009002010004002003006003008008004007002004006006004008003005011012010]
FEATURE [Part::Part2DObjectPython] Wire004  # Draft 2D object (typed FeaturePython)
  ChamferSize = 0
  Closed = true
  End = (-779.702,-32.2624,13.6839)
  FilletRadius = 0
  Length = 50.2599
  MakeFace = true
  Placement = pos=(-779.702,-16.5246,1.36605) rot=(0.57735,0.57735,0.57735;2.0944rad)
  Points = (4) [(0,0,0),(-1.25,-5,0),(-6.95164,-5,-3.41061e-13),(-15.7378,12.3178,-1.13687e-13)]
  Start = (-779.702,-16.5246,1.36605)
  Subdivisions = 0
FEATURE [Part::Extrusion] Extrusion043
  Base = -> Wire004
  Dir = (6.48488,-1.972e-13,-1.703e-13)
  DirMode = 0
  FaceMakerClass = Part::FaceMakerBullseye
  LengthFwd = 0
  LengthRev = 0
  Solid = true
  Symmetric = false
FEATURE [Part::Part2DObjectPython] Rectangle021  # Draft 2D object (typed FeaturePython)
  ChamferSize = 0
  Columns = 1
  FilletRadius = 0
  Height = 134
  Length = 54
  MakeFace = true
  Placement = pos=(-807.46,-1.86983,59.985) rot=(-1,0,0;1.81577rad)
  Rows = 1
  Support = -> [Extrusion043]
FEATURE [Part::FeaturePython] Slice009  # WARN: FeaturePython — macro-defined, semantics opaque (R4)
  Base = -> Fusion005002002014004003003002009002010004002003006003008008004007002004006006004008003005011012010
  Mode = 1
  Tolerance = 0
  Tools = -> [Rectangle021]
FEATURE [Part::FeaturePython] Slice009_child0  label="Slice009.0"  # WARN: FeaturePython — macro-defined, semantics opaque (R4)
  Base = -> Slice009
  FilterType = 1
  Invert = false
  OverrideMaxVal = 0
  WindowFrom = 80
  WindowTo = 100
  items = 0
FEATURE [Part::FeaturePython] Slice009_child1  label="Slice009.1"  # WARN: FeaturePython — macro-defined, semantics opaque (R4)
  Base = -> Slice009
  FilterType = 1
  Invert = false
  OverrideMaxVal = 0
  WindowFrom = 80
  WindowTo = 100
  items = 1
FEATURE [App::DocumentObjectGroup] GrExplode_Slice009  label="Exploded Slice009"
  Group = -> [Slice009_child0,Slice009_child1]
FEATURE [Part::Part2DObjectPython] Rectangle022  # Draft 2D object (typed FeaturePython)
  ChamferSize = 0
  Columns = 1
  FilletRadius = 0
  Height = 19
  Length = 1.4
  MakeFace = true
  Placement = pos=(-778.23,-8.62457,-2.63395) rot=(0.57735,0.57735,0.57735;2.0944rad)
  Rows = 1
FEATURE [Part::Extrusion] Extrusion044
  Base = -> Rectangle022
  Dir = (1,0,0)
  DirMode = 0
  FaceMakerClass = Part::FaceMakerBullseye
  LengthFwd = 0
  LengthRev = 0
  Solid = true
  Symmetric = false
FEATURE [Part::Feature] Face020
  Placement = pos=(-777.23,-8.62457,-2.63395) rot=(0.57735,0.57735,0.57735;2.0944rad)
  shape: bbox 6.713e-07 x 1.4 x 19 mm, 1 faces, 0 solids (baked)
FEATURE [Part::Extrusion] Extrusion045
  Base = -> Face020
  Dir = (-0.5,-1.15514e-08,-1.15514e-08)
  DirMode = 0
  FaceMakerClass = Part::FaceMakerBullseye
  LengthFwd = 0
  LengthRev = 0
  Solid = true
  Symmetric = false
FEATURE [Part::Cut] Cut004006005004002008019023005025020
  Base = -> Extrusion044
  Placement = pos=(21.0148,0,-4.62053e-09) rot=(0,0,1;0rad)
  Tool = -> Extrusion045
FEATURE [Part::Cut] Cut004006005004002008019023005025021
  Base = -> Extrusion044
  Tool = -> Extrusion045
FEATURE [Part::Feature] Face021
  Placement = pos=(0,-1.8e-15,-1) rot=(0,0,1;0rad)
  shape: bbox 2 x 5.5 x 7.594e-07 mm, 1 faces, 0 solids (baked)
FEATURE [Part::Extrusion] Extrusion046
  Base = -> Face021
  Dir = (0,0,-0.2)
  DirMode = 0
  FaceMakerClass = Part::FaceMakerBullseye
  LengthFwd = 0
  LengthRev = 0
  Solid = true
  Symmetric = false
FEATURE [Part::Cut] Cut004006005004002008019023005025022
  Base = -> Fusion005002002014004003003002009002010004002003006003008008004007002004006006004008003005011012008
  Tool = -> Extrusion046
FEATURE [Part::Feature] Face022
  shape: bbox 2 x 5 x 1.159e-06 mm, 1 faces, 0 solids (baked)
FEATURE [Part::Extrusion] Extrusion047
  Base = -> Face022
  Dir = (0,0,-0.2)
  DirMode = 0
  FaceMakerClass = Part::FaceMakerBullseye
  LengthFwd = 0
  LengthRev = 0
  Solid = true
  Symmetric = false
FEATURE [Part::Cut] Cut004006005004002008019023005025023
  Base = -> Cut004006005004002008019023005025022
  Tool = -> Extrusion047
FEATURE [App::DocumentObjectGroup] GrExplode_Slice005  label="Exploded Slice005"
  Group = -> [Cut004006005004002008019023005025023]
FEATURE [Part::Part2DObjectPython] Circle009  # Draft 2D object (typed FeaturePython)
  FirstAngle = 0
  LastAngle = 0
  MakeFace = true
  Placement = pos=(-767.462,-21.464,-3.63395) rot=(0,0,1;0rad)
  Radius = 2.60183
FEATURE [Part::Extrusion] Extrusion048
  Base = -> Circle009
  Dir = (4.2e-15,-7.8e-15,-3.5)
  DirMode = 0
  FaceMakerClass = Part::FaceMakerBullseye
  LengthFwd = 0
  LengthRev = 0
  Solid = true
  Symmetric = false
FEATURE [Part::MultiFuse] Fusion005002002014004003003002009002010004002003006003008008004007002004006006004008003005011012011
  Shapes = -> [Extrusion048,Slice008_child0]
FEATURE [App::DocumentObjectGroup] GrExplode_Slice008  label="Exploded Slice008"
  Group = -> [Slice008_child1,Fusion005002002014004003003002009002010004002003006003008008004007002004006006004008003005011012011]
FEATURE [Part::Feature] Slice003_child2001  label="Slice003.003"
  Placement = pos=(-92.9308,-3.446e-13,-2.93e-14) rot=(0,0,1;0rad)
  shape: bbox 20.5 x 4.601 x 23.5 mm, 12 faces (baked)
FEATURE [Part::Feature] Slice003_child2002  label="Slice003.004"
  shape: bbox 20.5 x 4.601 x 23.5 mm, 12 faces (baked)
FEATURE [Part::Feature] Face023
  Placement = pos=(-92.9308,-3.446e-13,-2.93e-14) rot=(0,0,1;0rad)
  shape: bbox 20.5 x 4.951e-06 x 23.5 mm, 1 faces, 0 solids (baked)
FEATURE [Part::Extrusion] Extrusion049
  Base = -> Face023
  Dir = (-5.82e-14,-20,-1.042e-13)
  DirMode = 0
  FaceMakerClass = Part::FaceMakerBullseye
  LengthFwd = 0
  LengthRev = 0
  Solid = true
  Symmetric = false
FEATURE [Part::Part2DObjectPython] Circle010  # Draft 2D object (typed FeaturePython)
  FirstAngle = 0
  LastAngle = 0
  MakeFace = true
  Placement = pos=(-782.324,-43.4762,16.3661) rot=(0.57735,-0.57735,-0.57735;2.0944rad)
  Radius = 20
FEATURE [Part::Extrusion] Extrusion050
  Base = -> Circle010
  Dir = (38.2881,0,0)
  DirMode = 0
  FaceMakerClass = Part::FaceMakerBullseye
  LengthFwd = 0
  LengthRev = 0
  Solid = true
  Symmetric = false
FEATURE [Part::Cut] Cut004006005004002008019023005025024
  Base = -> Extrusion049
  Tool = -> Extrusion050
FEATURE [Part::Part2DObjectPython] Rectangle023  # Draft 2D object (typed FeaturePython)
  ChamferSize = 0
  Columns = 1
  FilletRadius = 0
  Height = 20
  Length = 3.30507
  MakeFace = true
  Placement = pos=(-757.27,-23.4762,-3.63395) rot=(1,0,0;1.5708rad)
  Rows = 1
FEATURE [Part::Part2DObjectPython] Rectangle024  # Draft 2D object (typed FeaturePython)
  ChamferSize = 0
  Columns = 1
  FilletRadius = 0
  Height = 20
  Length = 3.18206
  MakeFace = true
  Placement = pos=(-780.952,-23.4762,-3.63395) rot=(1,0,0;1.5708rad)
  Rows = 1
  Support = -> [Fusion005002002014004003003002009002010004002003006003008008004007002004006006004008003005011012005]
FEATURE [Part::Extrusion] Extrusion051
  Base = -> Rectangle024
  Dir = (-3.04e-13,-20,-3.464e-13)
  DirMode = 0
  FaceMakerClass = Part::FaceMakerBullseye
  LengthFwd = 0
  LengthRev = 0
  Solid = true
  Symmetric = false
FEATURE [Part::Extrusion] Extrusion052
  Base = -> Rectangle023
  Dir = (-5.88e-14,-20,-1.021e-13)
  DirMode = 0
  FaceMakerClass = Part::FaceMakerBullseye
  LengthFwd = 0
  LengthRev = 0
  Solid = true
  Symmetric = false
FEATURE [Part::MultiFuse] Fusion005002002014004003003002009002010004002003006003008008004007002004006006004008003005011012012
  Shapes = -> [Extrusion052,Extrusion051]
FEATURE [Part::Part2DObjectPython] Circle011  # Draft 2D object (typed FeaturePython)
  FirstAngle = 0
  LastAngle = 0
  MakeFace = true
  Placement = pos=(-782.324,-43.4762,16.3661) rot=(0.57735,-0.57735,-0.57735;2.0944rad)
  Radius = 20
  Support = -> [Fusion005002002014004003003002009002010004002003006003008008004007002004006006004008003005011012011]
FEATURE [Part::Extrusion] Extrusion053
  Base = -> Circle011
  Dir = (34.3901,0,0)
  DirMode = 0
  FaceMakerClass = Part::FaceMakerBullseye
  LengthFwd = 0
  LengthRev = 0
  Solid = true
  Symmetric = false
FEATURE [Part::Cut] Cut004006005004002008019023005025025
  Base = -> Fusion005002002014004003003002009002010004002003006003008008004007002004006006004008003005011012012
  Tool = -> Extrusion053
FEATURE [Part::Part2DObjectPython] Rectangle025  # Draft 2D object (typed FeaturePython)
  ChamferSize = 0
  Columns = 1
  FilletRadius = 0
  Height = 4.60055
  Length = 3.30507
  MakeFace = true
  Placement = pos=(-757.27,-28.0768,16.3661) rot=(0,0,1;0rad)
  Rows = 1
  Support = -> [Slice003_child2001]
FEATURE [Part::Part2DObjectPython] Rectangle026  # Draft 2D object (typed FeaturePython)
  ChamferSize = 0
  Columns = 1
  FilletRadius = 0
  Height = 4.60055
  Length = 3.18206
  MakeFace = true
  Placement = pos=(-780.952,-28.0768,16.3661) rot=(0,0,1;0rad)
  Rows = 1
FEATURE [Part::Extrusion] Extrusion054
  Base = -> Rectangle025
  Dir = (-8.58e-14,6.02e-14,-10)
  DirMode = 0
  FaceMakerClass = Part::FaceMakerBullseye
  LengthFwd = 0
  LengthRev = 0
  Solid = true
  Symmetric = false
FEATURE [Part::Extrusion] Extrusion055
  Base = -> Rectangle026
  Dir = (-8.58e-14,6.02e-14,-10)
  DirMode = 0
  FaceMakerClass = Part::FaceMakerBullseye
  LengthFwd = 0
  LengthRev = 0
  Solid = true
  Symmetric = false
FEATURE [Part::Cut] Cut004006005004002008019023005025026
  Base = -> Cut004006005004002008019023005025025
  Tool = -> Extrusion054
FEATURE [Part::Cut] Cut004006005004002008019023005025027
  Base = -> Cut004006005004002008019023005025026
  Tool = -> Extrusion055
FEATURE [Part::MultiFuse] Fusion005002002014004003003002009002010004002003006003008008004007002004006006004008003005011012013
  Shapes = -> [Cut004006005004002008019023005025024,Cut004006005004002008019023005025027]
FEATURE [Part::MultiFuse] Fusion005002002014004003003002009002010004002003006003008008004007002004006006004008003005011012014
  Shapes = -> [Fusion005002002014004003003002009002010004002003006003008008004007002004006006004008003005011012013,Slice003_child2001]
FEATURE [Part::MultiFuse] Fusion005002002014004003003002009002010004002003006003008008004007002004006006004008003005011012015
  Shapes = -> [Slice006_child1,Fusion005002002014004003003002009002010004002003006003008008004007002004006006004008003005011012014]
FEATURE [App::DocumentObjectGroup] GrExplode_Slice006  label="Exploded Slice006"
  Group = -> [Slice006_child0,Fusion005002002014004003003002009002010004002003006003008008004007002004006006004008003005011012015]
